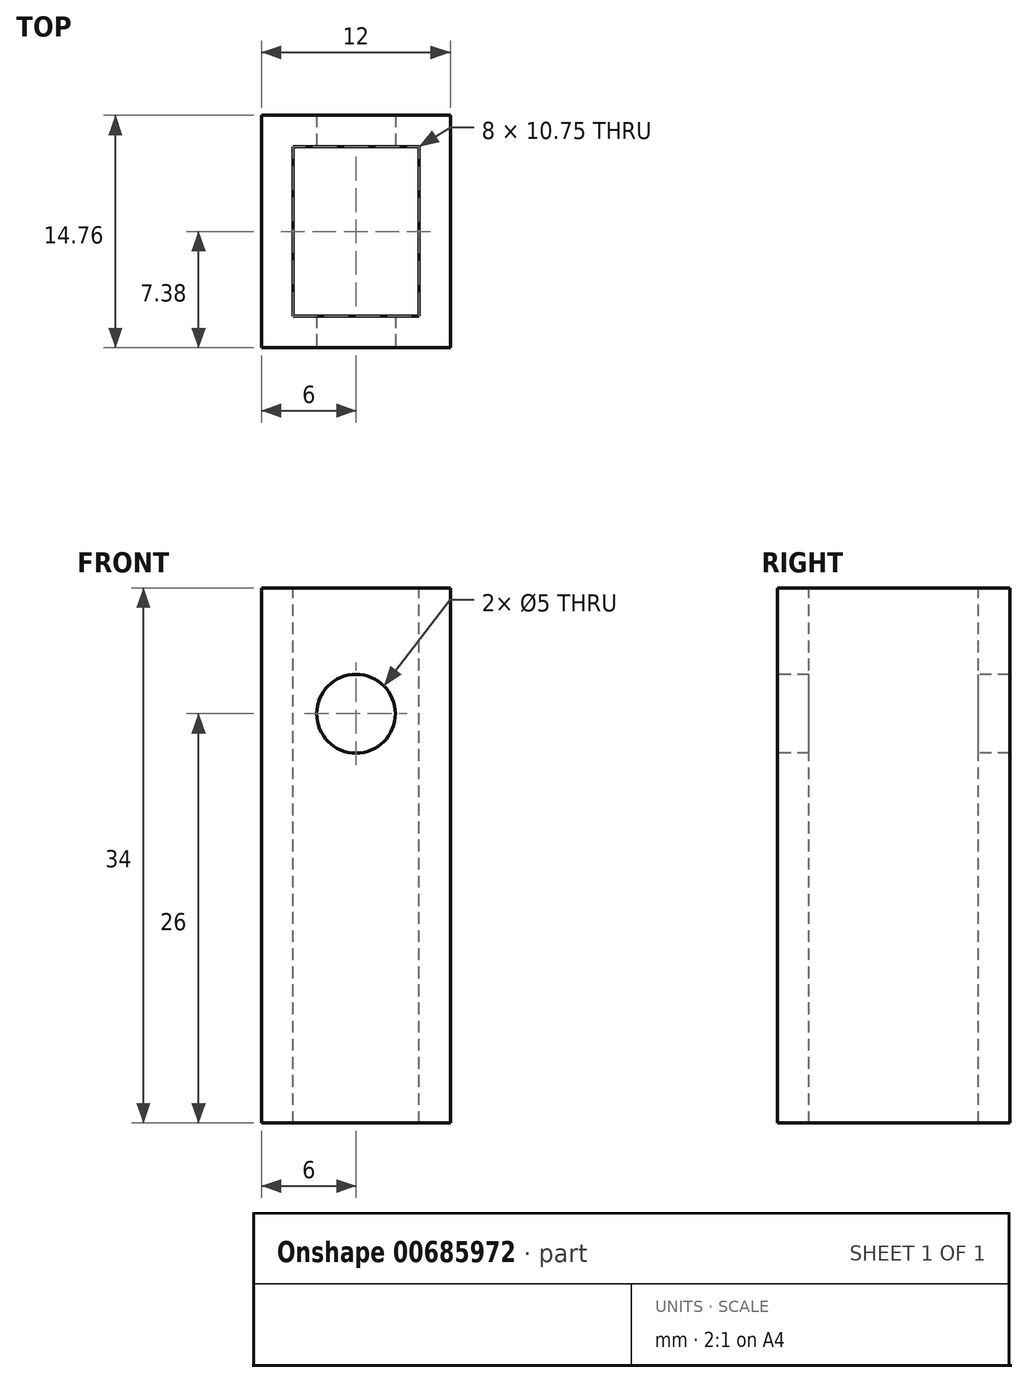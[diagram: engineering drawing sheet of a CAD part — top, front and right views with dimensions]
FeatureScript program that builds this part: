
annotation { "Feature Type Name" : "Feature", "Feature Type Description" : "" }
export const myFeature = defineFeature(function(context is Context, id is Id, definition is map)
    precondition{}
    {
        {
            var Q0;
            Q0=qCreatedBy(makeId("Top.planeOp"),FACE);
            var sketch = newSketch(context, id + "F0", { "sketchPlane" : qUnion([Q0])});
            skLineSegment(sketch, "E0.bottom", {"start": v(6, -7.38) * mm, "end": v(-6, -7.38) * mm});
            skLineSegment(sketch, "E0.top", {"start": v(6, 7.38) * mm, "end": v(-6, 7.38) * mm});
            skLineSegment(sketch, "E0.left", {"start": v(6, -7.38) * mm, "end": v(6, 7.38) * mm});
            skLineSegment(sketch, "E0.right", {"start": v(-6, -7.38) * mm, "end": v(-6, 7.38) * mm});
            skPoint(sketch, "E0.middle", {"position": v(0, 0) * mm});
            skSolve(sketch);
        }
        {
            var Q0;
            Q0=makeQuery(id+"F0.imprint","IMPRINT",FACE,{"disambiguationData":[TD([[makeQuery(id+"F0.imprint","IMPRINT",EDGE,{"derivedFrom":sQuery(id+"F0.wireOp",EDGE,"E0.bottom")}),-1.0]])]});
            extrude(context, id + "F1", {"entities" : qUnion([Q0]), "oppositeDirection" : true, "depth" : 34 * mm, "offsetDistance" : 25 * mm});
        }
        {
            var Q0;
            Q0=makeQuery(id+"F1.opExtrude","CAP_FACE",FACE,{"disambiguationData":[OSD([sQuery(id+"F0.wireOp",EDGE,"E0.bottom"),sQuery(id+"F0.wireOp",EDGE,"E0.top"),sQuery(id+"F0.wireOp",EDGE,"E0.left"),sQuery(id+"F0.wireOp",EDGE,"E0.right")])],"isStart":true});
            var sketch = newSketch(context, id + "F2", { "sketchPlane" : qUnion([Q0])});
            skLineSegment(sketch, "E1.bottom", {"start": v(-4, 5.38) * mm, "end": v(4, 5.38) * mm});
            skLineSegment(sketch, "E1.top", {"start": v(-4, -5.38) * mm, "end": v(4, -5.38) * mm});
            skLineSegment(sketch, "E1.left", {"start": v(-4, 5.38) * mm, "end": v(-4, -5.38) * mm});
            skLineSegment(sketch, "E1.right", {"start": v(4, 5.38) * mm, "end": v(4, -5.38) * mm});
            skPoint(sketch, "E1.middle", {"position": v(0, 0) * mm});
            skSolve(sketch);
        }
        {
            var Q0;
            Q0=makeQuery(id+"F2.imprint","IMPRINT",FACE,{"disambiguationData":[TD([[makeQuery(id+"F2.imprint","IMPRINT",EDGE,{"derivedFrom":sQuery(id+"F2.wireOp",EDGE,"E1.bottom")}),-1.0]])]});
            extrude(context, id + "F3", {"entities" : qUnion([Q0]), "operationType" : NewBodyOperationType.REMOVE, "oppositeDirection" : true, "depth" : 36 * mm, "offsetDistance" : 25 * mm});
        }
        {
            var Q0;
            Q0=makeQuery(id+"F1.opExtrude","SWEPT_FACE",FACE,{"disambiguationData":[OSD([sQuery(id+"F0.wireOp",EDGE,"E0.bottom")])]});
            var sketch = newSketch(context, id + "F4", { "sketchPlane" : qUnion([Q0])});
            skPoint(sketch, "E2", {"position": v(0, -8) * mm});
            skSolve(sketch);
        }
        {
            var Q0;
            Q0=sQuery(id+"F4.wireOp",VERTEX,"E2");
            var Q1;
            Q1=makeQuery(id+"F1.opExtrude","SWEPT_BODY",BODY,{"disambiguationData":[OSD([sQuery(id+"F0.wireOp",EDGE,"E0.bottom"),sQuery(id+"F0.wireOp",EDGE,"E0.top"),sQuery(id+"F0.wireOp",EDGE,"E0.left"),sQuery(id+"F0.wireOp",EDGE,"E0.right")])]});
            hole(context, id + "F5", {"style" : HoleStyle.SIMPLE, "endStyle" : HoleEndStyle.THROUGH, "holeDiameter" : 5 * mm, "majorDiameter" : 5 * mm, "isTappedThrough" : true, "tappedDepth" : 12 * mm, "tapClearance" : 3, "locations" : qUnion([Q0]), "scope" : qUnion([Q1])});
        }
    });
